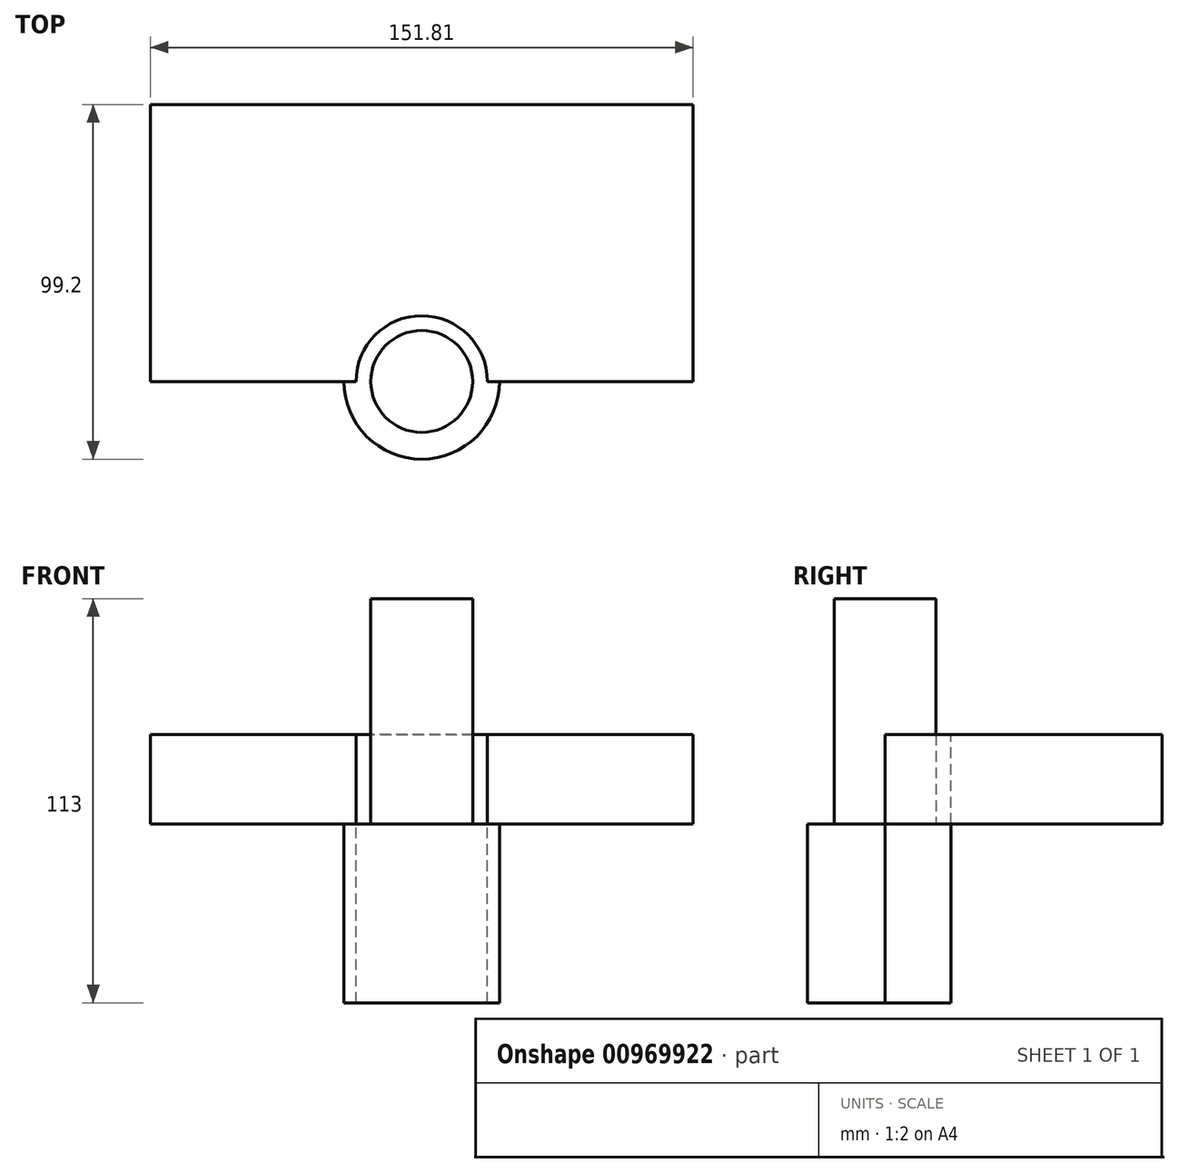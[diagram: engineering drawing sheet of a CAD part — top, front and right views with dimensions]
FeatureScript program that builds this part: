
annotation { "Feature Type Name" : "Feature", "Feature Type Description" : "" }
export const myFeature = defineFeature(function(context is Context, id is Id, definition is map)
    precondition{}
    {
        {
            var Q0;
            Q0=qCreatedBy(makeId("Top.planeOp"),FACE);
            var sketch = newSketch(context, id + "F0", { "sketchPlane" : qUnion([Q0])});
            skLineSegment(sketch, "E0.bottom", {"start": v(-69.13, 37.76) * mm, "end": v(82.68, 37.76) * mm});
            skLineSegment(sketch, "E0.top", {"start": v(-69.13, -39.7) * mm, "end": v(82.68, -39.7) * mm});
            skLineSegment(sketch, "E0.left", {"start": v(-69.13, 37.76) * mm, "end": v(-69.13, -39.7) * mm});
            skLineSegment(sketch, "E0.right", {"start": v(82.68, 37.76) * mm, "end": v(82.68, -39.7) * mm});
            skSolve(sketch);
        }
        {
            var Q0;
            Q0 = qSketchRegion(id + "F0", true);
            extrude(context, id + "F1", {"entities" : qUnion([Q0]), "depth" : 25 * mm, "offsetDistance" : 25 * mm});
        }
        {
            var Q0;
            Q0=makeQuery(id+"F1.opExtrude","CAP_FACE",FACE,{"disambiguationData":[OSD([sQuery(id+"F0.wireOp",EDGE,"E0.bottom"),sQuery(id+"F0.wireOp",EDGE,"E0.top"),sQuery(id+"F0.wireOp",EDGE,"E0.left"),sQuery(id+"F0.wireOp",EDGE,"E0.right")])],"isStart":false});
            var sketch = newSketch(context, id + "F2", { "sketchPlane" : qUnion([Q0])});
            skCircle(sketch, "E1", {"center": v(6.78, -39.7) * mm, "radius": 18.37 * mm});
            skSolve(sketch);
        }
        {
            var Q0;
            {var subQ0=sQuery(id+"F2.wireOp",EDGE,"E1");var subQ1=makeQuery(id+"F1.opExtrude","CAP_EDGE",EDGE,{"disambiguationData":[OSD([sQuery(id+"F0.wireOp",EDGE,"E0.top")])],"isStart":false});var subQ2=makeQuery(id+"F2.imprint","INTERSECT",VERTEX,{"disambiguationData":[OD(0.0)],"derivedFrom":[subQ1,subQ0]});Q0=makeQuery(id+"F2.imprint","IMPRINT",FACE,{"disambiguationData":[TD([[makeQuery(id+"F2.imprint","IMPRINT",EDGE,{"disambiguationData":[TD([[subQ2,1.0]])],"derivedFrom":subQ0}),1.0]])]});}
            extrude(context, id + "F3", {"entities" : qUnion([Q0]), "operationType" : NewBodyOperationType.REMOVE, "oppositeDirection" : true, "depth" : 25 * mm, "offsetDistance" : 25 * mm});
        }
        {
            var Q0;
            Q0=makeQuery(id+"F1.opExtrude","CAP_FACE",FACE,{"disambiguationData":[OSD([sQuery(id+"F0.wireOp",EDGE,"E0.bottom"),sQuery(id+"F0.wireOp",EDGE,"E0.top"),sQuery(id+"F0.wireOp",EDGE,"E0.left"),sQuery(id+"F0.wireOp",EDGE,"E0.right")])],"isStart":true});
            var sketch = newSketch(context, id + "F4", { "sketchPlane" : qUnion([Q0])});
            skCircle(sketch, "E2", {"center": v(6.78, 39.7) * mm, "radius": 15.36 * mm});
            skCircle(sketch, "E3", {"center": v(6.78, 39.7) * mm, "radius": 21.75 * mm});
            skSolve(sketch);
        }
        {
            var Q0;
            Q0=makeQuery(id+"F4.imprint","IMPRINT",FACE,{"disambiguationData":[TD([[makeQuery(id+"F4.imprint","IMPRINT",EDGE,{"derivedFrom":sQuery(id+"F4.wireOp",EDGE,"E2")}),1.0]])]});
            var Q1;
            Q1=makeQuery(id+"F4.imprint","IMPRINT",FACE,{"disambiguationData":[TD([[makeQuery(id+"F4.imprint","IMPRINT",EDGE,{"derivedFrom":sQuery(id+"F4.wireOp",EDGE,"E2")}),-1.0]])]});
            extrude(context, id + "F5", {"entities" : qUnion([Q0, Q1]), "depth" : 50 * mm, "offsetDistance" : 25 * mm});
        }
        {
            var Q0;
            Q0=makeQuery(id+"F5.opExtrude","CAP_FACE",FACE,{"disambiguationData":[OSD([sQuery(id+"F0.wireOp",EDGE,"E0.top"),sQuery(id+"F2.wireOp",EDGE,"E1"),sQuery(id+"F4.wireOp",EDGE,"E3")])],"isStart":true});
            var sketch = newSketch(context, id + "F6", { "sketchPlane" : qUnion([Q0])});
            skCircle(sketch, "E4", {"center": v(6.78, -39.7) * mm, "radius": 14.23 * mm});
            skSolve(sketch);
        }
        {
            var Q0;
            Q0 = qSketchRegion(id + "F6", true);
            extrude(context, id + "F7", {"entities" : qUnion([Q0]), "operationType" : NewBodyOperationType.ADD, "depth" : 63 * mm, "offsetDistance" : 25 * mm});
        }
    });
